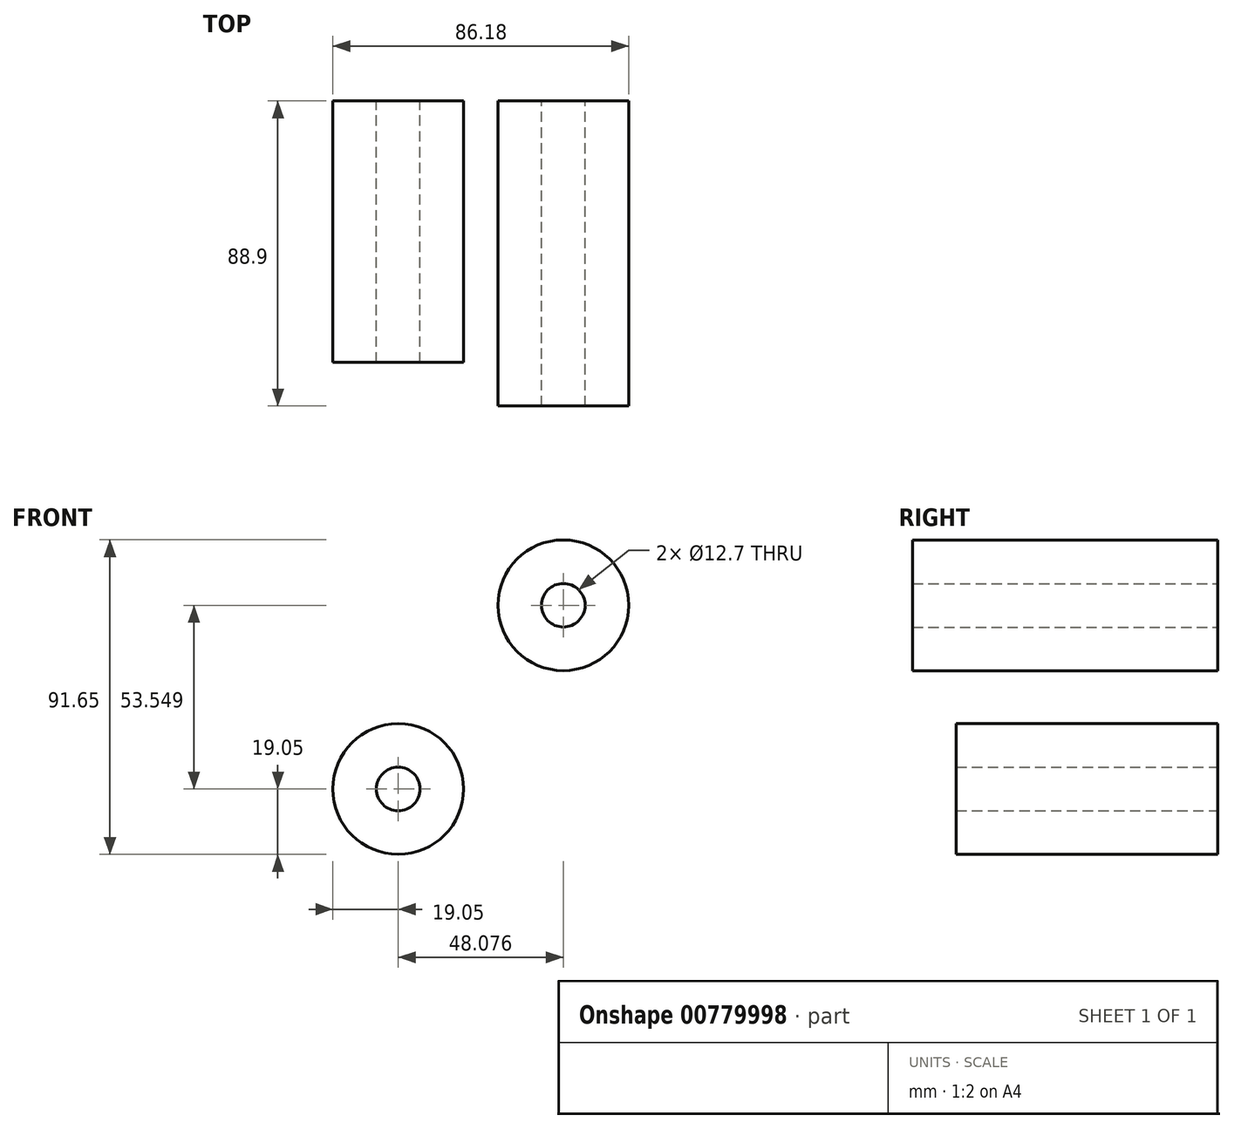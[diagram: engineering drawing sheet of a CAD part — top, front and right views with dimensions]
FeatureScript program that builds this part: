
annotation { "Feature Type Name" : "Feature", "Feature Type Description" : "" }
export const myFeature = defineFeature(function(context is Context, id is Id, definition is map)
    precondition{}
    {
        {
            var Q0;
            Q0=qCreatedBy(makeId("Front.planeOp"),FACE);
            var sketch = newSketch(context, id + "F0", { "sketchPlane" : qUnion([Q0])});
            skCircle(sketch, "E0", {"center": v(0, 0) * mm, "radius": 6.35 * mm});
            skCircle(sketch, "E1", {"center": v(0, 0) * mm, "radius": 19.05 * mm});
            skSolve(sketch);
        }
        {
            var Q0;
            Q0 = qSketchRegion(id + "F0", true);
            var Q1;
            Q1=makeQuery(id+"F0.imprint","IMPRINT",FACE,{"disambiguationData":[TD([[makeQuery(id+"F0.imprint","IMPRINT",EDGE,{"derivedFrom":sQuery(id+"F0.wireOp",EDGE,"E0")}),-1.0]])]});
            extrude(context, id + "F1", {"entities" : qUnion([Q0, Q1]), "depth" : 76.2 * mm, "offsetDistance" : 25.4 * mm});
        }
        {
            var Q0;
            Q0=qCreatedBy(makeId("Front.planeOp"),FACE);
            var sketch = newSketch(context, id + "F2", { "sketchPlane" : qUnion([Q0])});
            skCircle(sketch, "E2", {"center": v(48.08, 53.55) * mm, "radius": 6.35 * mm});
            skCircle(sketch, "E3", {"center": v(48.08, 53.55) * mm, "radius": 19.05 * mm});
            skSolve(sketch);
        }
        {
            var Q0;
            Q0 = qSketchRegion(id + "F2", true);
            extrude(context, id + "F3", {"entities" : qUnion([Q0]), "depth" : 88.9 * mm, "offsetDistance" : 25.4 * mm});
        }
    });
